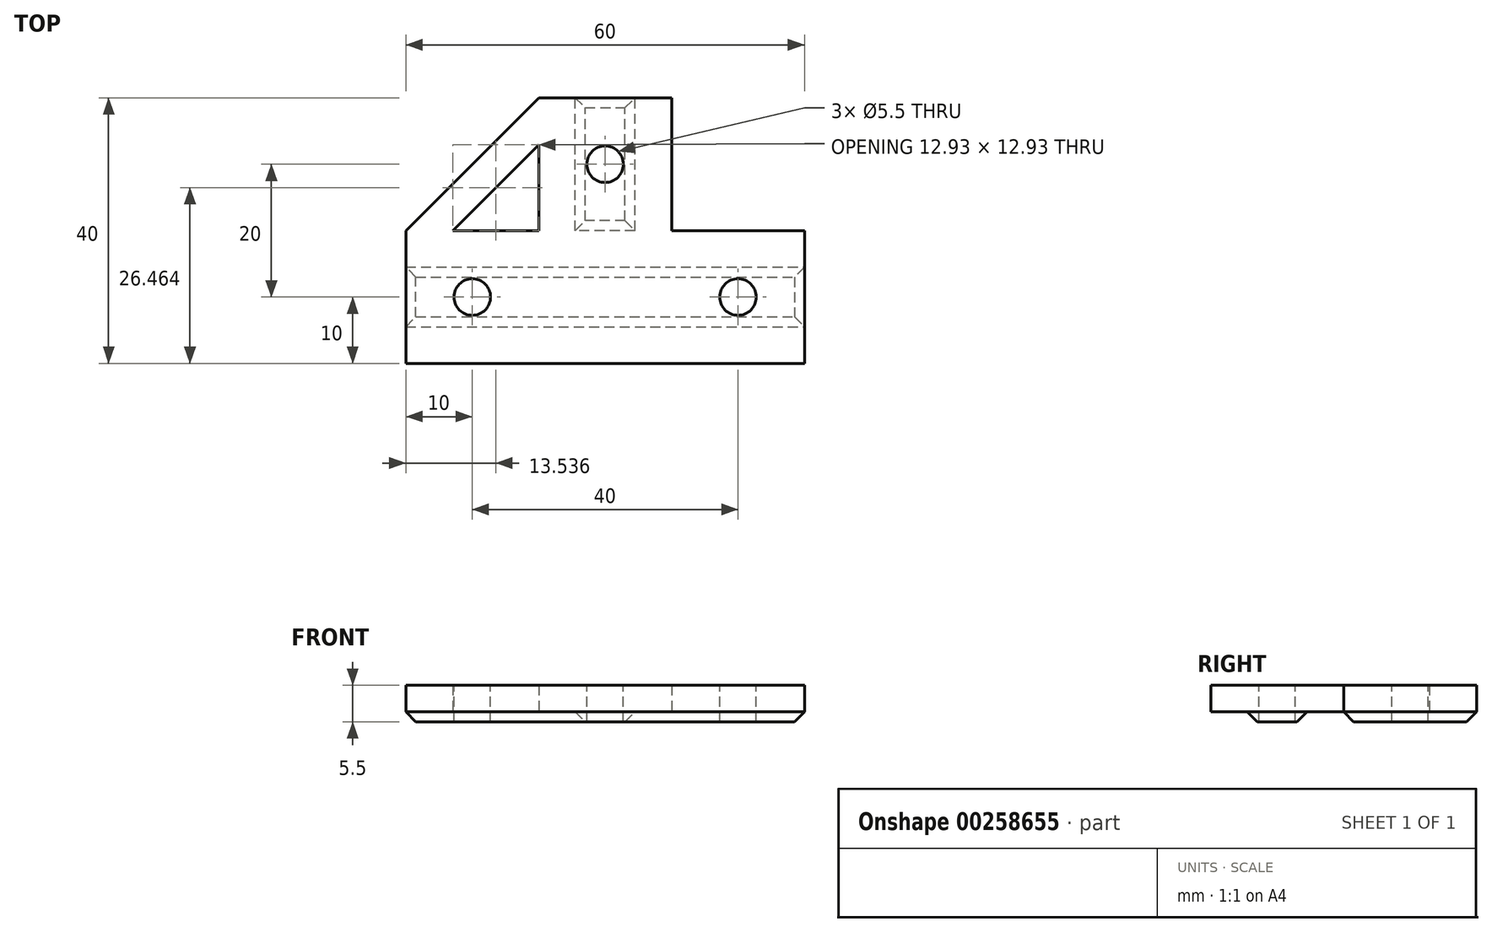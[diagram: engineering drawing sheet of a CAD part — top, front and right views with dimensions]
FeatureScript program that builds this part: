
annotation { "Feature Type Name" : "Feature", "Feature Type Description" : "" }
export const myFeature = defineFeature(function(context is Context, id is Id, definition is map)
    precondition{}
    {
        {
            var Q0;
            Q0=qCreatedBy(makeId("Top.planeOp"),FACE);
            var sketch = newSketch(context, id + "F0", { "sketchPlane" : qUnion([Q0])});
            skLineSegment(sketch, "E0", {"start": v(0, 0) * mm, "end": v(60, 0) * mm});
            skLineSegment(sketch, "E1", {"start": v(60, 0) * mm, "end": v(60, 20) * mm});
            skLineSegment(sketch, "E2", {"start": v(60, 20) * mm, "end": v(40, 20) * mm});
            skLineSegment(sketch, "E3", {"start": v(40, 20) * mm, "end": v(40, 40) * mm});
            skLineSegment(sketch, "E4", {"start": v(40, 40) * mm, "end": v(20, 40) * mm});
            skLineSegment(sketch, "E5", {"start": v(20, 40) * mm, "end": v(0, 20) * mm});
            skPoint(sketch, "E5.endSnap0", {"position": v(50, 20) * mm});
            skLineSegment(sketch, "E6", {"start": v(0, 20) * mm, "end": v(0, 0) * mm});
            skLineSegment(sketch, "E7", {"start": v(20, 20) * mm, "end": v(20, 32.93) * mm});
            skLineSegment(sketch, "E8", {"start": v(20, 32.93) * mm, "end": v(7.07, 20) * mm});
            skLineSegment(sketch, "E9", {"start": v(7.07, 20) * mm, "end": v(20, 20) * mm});
            skPoint(sketch, "E10.centerSnap0", {"position": v(0, 10) * mm});
            skPoint(sketch, "E11.centerSnap0", {"position": v(30, 40) * mm});
            skSolve(sketch);
        }
        {
            var Q0;
            Q0 = qSketchRegion(id + "F0", true);
            extrude(context, id + "F1", {"entities" : qUnion([Q0]), "depth" : 4 * mm});
        }
        {
            var Q0;
            Q0=makeQuery(id+"F1.opExtrude","SWEPT_FACE",FACE,{"disambiguationData":[OSD([sQuery(id+"F0.wireOp",EDGE,"E1")])]});
            var sketch = newSketch(context, id + "F2", { "sketchPlane" : qUnion([Q0])});
            skLineSegment(sketch, "E12", {"start": v(5.5, 0) * mm, "end": v(7, -1.5) * mm});
            skLineSegment(sketch, "E13", {"start": v(7, -1.5) * mm, "end": v(13, -1.5) * mm});
            skLineSegment(sketch, "E14", {"start": v(13, -1.5) * mm, "end": v(14.5, 0) * mm});
            skLineSegment(sketch, "E15", {"start": v(14.5, 0) * mm, "end": v(5.5, 0) * mm});
            skSolve(sketch);
        }
        {
            var Q0;
            Q0 = qSketchRegion(id + "F2", true);
            var Q1;
            Q1=makeQuery(id+"F1.opExtrude","SWEPT_FACE",FACE,{"disambiguationData":[OSD([sQuery(id+"F0.wireOp",EDGE,"E6")])]});
            extrude(context, id + "F3", {"entities" : qUnion([Q0]), "operationType" : NewBodyOperationType.ADD, "endBound" : BoundingType.UP_TO_SURFACE, "oppositeDirection" : true, "endBoundEntityFace" : qUnion([Q1]), "depth" : 25 * mm});
        }
        {
            var Q0;
            Q0=makeQuery(id+"F1.opExtrude","SWEPT_FACE",FACE,{"disambiguationData":[OSD([sQuery(id+"F0.wireOp",EDGE,"E4")])]});
            var sketch = newSketch(context, id + "F4", { "sketchPlane" : qUnion([Q0])});
            skLineSegment(sketch, "E16", {"start": v(-34.5, 0) * mm, "end": v(-33, -1.5) * mm});
            skLineSegment(sketch, "E17", {"start": v(-33, -1.5) * mm, "end": v(-27, -1.5) * mm});
            skLineSegment(sketch, "E18", {"start": v(-27, -1.5) * mm, "end": v(-25.5, 0) * mm});
            skLineSegment(sketch, "E19", {"start": v(-25.5, 0) * mm, "end": v(-34.5, 0) * mm});
            skSolve(sketch);
        }
        {
            var Q0;
            Q0 = qSketchRegion(id + "F4", true);
            var Q1;
            Q1=makeQuery(id+"F1.opExtrude","SWEPT_FACE",FACE,{"disambiguationData":[OSD([sQuery(id+"F0.wireOp",EDGE,"E2")])]});
            extrude(context, id + "F5", {"entities" : qUnion([Q0]), "operationType" : NewBodyOperationType.ADD, "endBound" : BoundingType.UP_TO_SURFACE, "oppositeDirection" : true, "endBoundEntityFace" : qUnion([Q1]), "depth" : 25 * mm});
        }
        {
            var Q0;
            Q0=makeQuery(id+"F3.opExtrude","CAP_EDGE",EDGE,{"disambiguationData":[OSD([sQuery(id+"F2.wireOp",EDGE,"E13")])],"isStart":true});
            var Q1;
            Q1=makeQuery(id+"F3.opExtrude","CAP_EDGE",EDGE,{"disambiguationData":[OSD([sQuery(id+"F2.wireOp",EDGE,"E13")])],"isStart":false});
            var Q2;
            Q2=makeQuery(id+"F5.opExtrude","CAP_EDGE",EDGE,{"disambiguationData":[OSD([sQuery(id+"F4.wireOp",EDGE,"E17")])],"isStart":false});
            var Q3;
            Q3=makeQuery(id+"F5.opExtrude","CAP_EDGE",EDGE,{"disambiguationData":[OSD([sQuery(id+"F4.wireOp",EDGE,"E17")])],"isStart":true});
            chamfer(context, id + "F6", {"entities" : qUnion([Q0, Q1, Q2, Q3]), "width" : 1.5 * mm, "tangentPropagation" : true});
        }
        {
            var Q0;
            Q0=makeQuery(id+"F1.opExtrude","CAP_FACE",FACE,{"disambiguationData":[OSD([sQuery(id+"F0.wireOp",EDGE,"E0"),sQuery(id+"F0.wireOp",EDGE,"E1"),sQuery(id+"F0.wireOp",EDGE,"E2"),sQuery(id+"F0.wireOp",EDGE,"E3"),sQuery(id+"F0.wireOp",EDGE,"E4"),sQuery(id+"F0.wireOp",EDGE,"E5"),sQuery(id+"F0.wireOp",EDGE,"E6"),sQuery(id+"F0.wireOp",EDGE,"E7"),sQuery(id+"F0.wireOp",EDGE,"E8"),sQuery(id+"F0.wireOp",EDGE,"E9")])],"isStart":false});
            var sketch = newSketch(context, id + "F7", { "sketchPlane" : qUnion([Q0])});
            skCircle(sketch, "E20", {"center": v(30, 30) * mm, "radius": 2.75 * mm});
            skPoint(sketch, "E20.centerSnap0", {"position": v(30, 40) * mm});
            skCircle(sketch, "E21", {"center": v(10, 10) * mm, "radius": 2.75 * mm});
            skPoint(sketch, "E21.centerSnap0", {"position": v(0, 10) * mm});
            skCircle(sketch, "E22", {"center": v(50, 10) * mm, "radius": 2.75 * mm});
            skPoint(sketch, "E22.centerSnap0", {"position": v(60, 10) * mm});
            skSolve(sketch);
        }
        {
            var Q0;
            Q0 = qSketchRegion(id + "F7", true);
            extrude(context, id + "F8", {"entities" : qUnion([Q0]), "operationType" : NewBodyOperationType.REMOVE, "endBound" : BoundingType.THROUGH_ALL, "oppositeDirection" : true, "depth" : 25 * mm});
        }
    });
